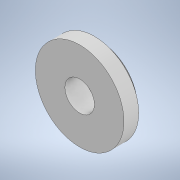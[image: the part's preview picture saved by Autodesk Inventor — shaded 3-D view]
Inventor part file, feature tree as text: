
AUTODESK INVENTOR PART (.ipt)
format: ipt  version: 2022 (Build 260153000, 153)  size: 116,736 bytes
history: native  units: in
note: dims shown in document units (in); Inventor stores cm internally (conversion verified against a paired STEP export)
features: extrude x3, sketch x3
ambient origin geometry x8: Origin, YZ Plane, XZ Plane, XY Plane, X Axis, Y Axis, Z Axis, Center Point
bodies: Solid1 (feature_tree)
feature tree (6):
  extrude  "Extrusion1"  Depth=0.1969in TaperAngle=0.0deg
  extrude  "Extrusion2"  Depth=0.2756in TaperAngle=0.0deg
  extrude  "Extrusion3"  Depth=0.2756in TaperAngle=0.0deg
  sketch  "Sketch2"  dims[d0=1.1811in d1=0.1969in d2=0.0in]
  sketch  "Sketch3"  dims[d3=0.9843in d4=0.2756in d5=0.0in]
  sketch  "Sketch4"  dims[d6=0.3937in d7=0.2756in d8=0.0in]
